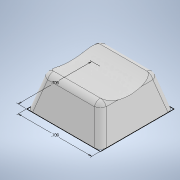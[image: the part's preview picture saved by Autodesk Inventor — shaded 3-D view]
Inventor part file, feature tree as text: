
AUTODESK INVENTOR PART (.ipt)
format: ipt  version: 2022 (Build 260153000, 153)  size: 198,144 bytes
history: native  units: in
note: dims shown in document units (in); Inventor stores cm internally (conversion verified against a paired STEP export)
features: extrude x5, sketch x5, fillet x1, plane x1
ambient origin geometry x8: Origin, YZ Plane, XZ Plane, XY Plane, X Axis, Y Axis, Z Axis, Center Point
bodies: Solid1 (feature_tree)
feature tree (12):
  extrude  "Extrusion1"  Depth=0.7087in
  fillet  "Fillet1"  Radius=0.315in
  plane  "Work Plane1"
  extrude  "Extrusion2"  Depth=0.4724in
  extrude  "Extrusion3"  Depth=0.6299in
  extrude  "Extrusion4"  Depth=0.1772in
  extrude  "Extrusion5"  Depth=0.1575in TaperAngle=0.0deg
  sketch  "Sketch1"  dims[d0=0.7087in d1=0.7087in d2=0.315in d3=-0.1031in]
  sketch  "Sketch2"  dims[d4=0.0591in d5=0.4724in]
  sketch  "Sketch3"  dims[d6=0.0in d7=0.0in d8=0.6299in]
  sketch  "Sketch4"  dims[d9=0.6299in d10=0.1772in d11=-0.1031in]
  sketch  "Sketch5"  dims[d12=0.2185in d13=0.1575in d14=0.0in d15=0.125in d16=0.1634in d17=0.1634in d18=0.125in d20=0.1575in d21=0.0in]
